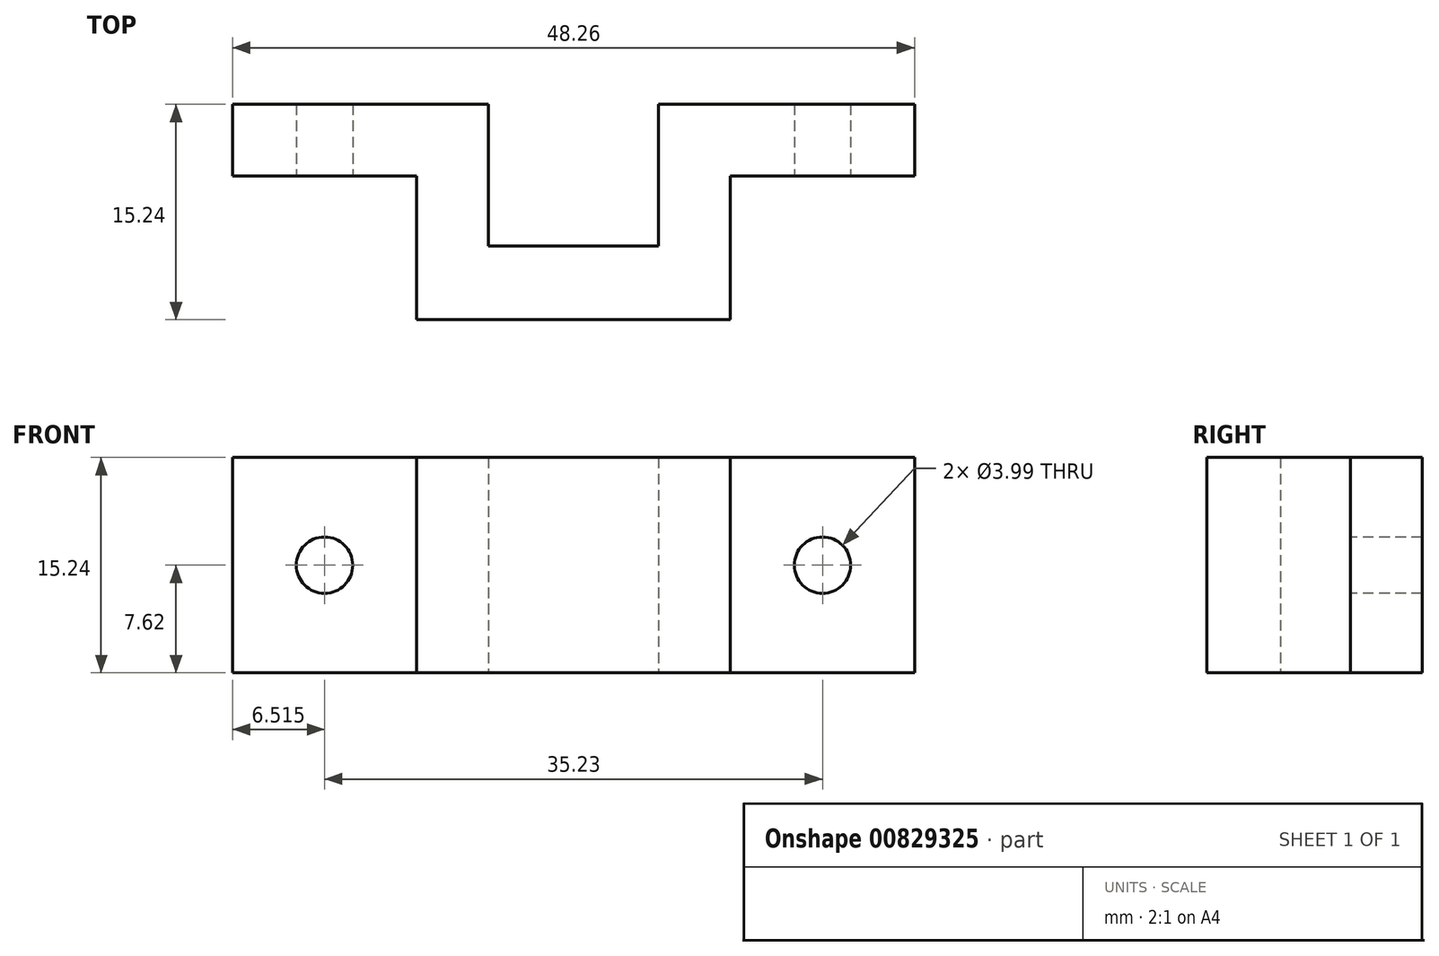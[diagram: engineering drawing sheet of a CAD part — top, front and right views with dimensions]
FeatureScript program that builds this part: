
annotation { "Feature Type Name" : "Feature", "Feature Type Description" : "" }
export const myFeature = defineFeature(function(context is Context, id is Id, definition is map)
    precondition{}
    {
        {
            var Q0;
            Q0=qCreatedBy(makeId("Front.planeOp"),FACE);
            var sketch = newSketch(context, id + "F0", { "sketchPlane" : qUnion([Q0])});
            skLineSegment(sketch, "E0.bottom", {"start": v(-24.13, 7.62) * mm, "end": v(24.13, 7.62) * mm});
            skLineSegment(sketch, "E0.top", {"start": v(-24.13, -7.62) * mm, "end": v(24.13, -7.62) * mm});
            skLineSegment(sketch, "E0.left", {"start": v(-24.13, 7.62) * mm, "end": v(-24.13, -7.62) * mm});
            skLineSegment(sketch, "E0.right", {"start": v(24.13, 7.62) * mm, "end": v(24.13, -7.62) * mm});
            skSolve(sketch);
        }
        {
            var Q0;
            Q0=makeQuery(id+"F0.imprint","IMPRINT",FACE,{"disambiguationData":[TD([[makeQuery(id+"F0.imprint","IMPRINT",EDGE,{"derivedFrom":sQuery(id+"F0.wireOp",EDGE,"E0.bottom")}),-1.0]])]});
            extrude(context, id + "F1", {"entities" : qUnion([Q0]), "depth" : 15.24 * mm, "offsetDistance" : 25.4 * mm});
        }
        {
            var Q0;
            Q0=makeQuery(id+"F1.opExtrude","SWEPT_FACE",FACE,{"disambiguationData":[OSD([sQuery(id+"F0.wireOp",EDGE,"E0.top")])]});
            var sketch = newSketch(context, id + "F2", { "sketchPlane" : qUnion([Q0])});
            skLineSegment(sketch, "E1.bottom", {"start": v(-6.02, 0) * mm, "end": v(6.02, 0) * mm});
            skLineSegment(sketch, "E1.top", {"start": v(-6.02, 10.03) * mm, "end": v(6.02, 10.03) * mm});
            skLineSegment(sketch, "E1.left", {"start": v(-6.02, 0) * mm, "end": v(-6.02, 10.03) * mm});
            skLineSegment(sketch, "E1.right", {"start": v(6.02, 0) * mm, "end": v(6.02, 10.03) * mm});
            skSolve(sketch);
        }
        {
            var Q0;
            Q0 = qSketchRegion(id + "F2", true);
            extrude(context, id + "F3", {"entities" : qUnion([Q0]), "operationType" : NewBodyOperationType.REMOVE, "oppositeDirection" : true, "depth" : 15.24 * mm, "offsetDistance" : 25.4 * mm});
        }
        {
            var Q0;
            Q0=makeQuery(id+"F1.opExtrude","SWEPT_FACE",FACE,{"disambiguationData":[OSD([sQuery(id+"F0.wireOp",EDGE,"E0.top")])]});
            var sketch = newSketch(context, id + "F4", { "sketchPlane" : qUnion([Q0])});
            skLineSegment(sketch, "E2.bottom", {"start": v(11.1, 15.24) * mm, "end": v(24.13, 15.24) * mm});
            skLineSegment(sketch, "E2.top", {"start": v(11.1, 5.07) * mm, "end": v(24.13, 5.07) * mm});
            skLineSegment(sketch, "E2.left", {"start": v(11.1, 15.24) * mm, "end": v(11.1, 5.07) * mm});
            skLineSegment(sketch, "E2.right", {"start": v(24.13, 15.24) * mm, "end": v(24.13, 5.07) * mm});
            skSolve(sketch);
        }
        {
            var Q0;
            Q0 = qSketchRegion(id + "F4", true);
            extrude(context, id + "F5", {"entities" : qUnion([Q0]), "operationType" : NewBodyOperationType.REMOVE, "oppositeDirection" : true, "depth" : 15.24 * mm, "offsetDistance" : 25.4 * mm});
        }
        {
            var Q0;
            Q0=makeQuery(id+"F1.opExtrude","SWEPT_FACE",FACE,{"disambiguationData":[OSD([sQuery(id+"F0.wireOp",EDGE,"E0.top")])]});
            var sketch = newSketch(context, id + "F6", { "sketchPlane" : qUnion([Q0])});
            skLineSegment(sketch, "E3.bottom", {"start": v(-24.13, 15.24) * mm, "end": v(-11.1, 15.24) * mm});
            skLineSegment(sketch, "E3.top", {"start": v(-24.13, 5.07) * mm, "end": v(-11.1, 5.07) * mm});
            skLineSegment(sketch, "E3.left", {"start": v(-24.13, 15.24) * mm, "end": v(-24.13, 5.07) * mm});
            skLineSegment(sketch, "E3.right", {"start": v(-11.1, 15.24) * mm, "end": v(-11.1, 5.07) * mm});
            skSolve(sketch);
        }
        {
            var Q0;
            Q0 = qSketchRegion(id + "F6", true);
            extrude(context, id + "F7", {"entities" : qUnion([Q0]), "operationType" : NewBodyOperationType.REMOVE, "oppositeDirection" : true, "depth" : 25.4 * mm, "offsetDistance" : 25.4 * mm});
        }
        {
            var Q0;
            Q0=makeQuery(id+"F7.boolean.opBoolean","COPY",FACE,{"derivedFrom":makeQuery(id+"F7.opExtrude","SWEPT_FACE",FACE,{"disambiguationData":[OSD([sQuery(id+"F6.wireOp",EDGE,"E3.top")])]})});
            var sketch = newSketch(context, id + "F8", { "sketchPlane" : qUnion([Q0])});
            skCircle(sketch, "E4", {"center": v(-17.61, 0) * mm, "radius": 2 * mm});
            skSolve(sketch);
        }
        {
            var Q0;
            Q0 = qSketchRegion(id + "F8", true);
            extrude(context, id + "F9", {"entities" : qUnion([Q0]), "operationType" : NewBodyOperationType.REMOVE, "oppositeDirection" : true, "depth" : 5.08 * mm, "offsetDistance" : 25.4 * mm});
        }
        {
            var Q0;
            Q0=makeQuery(id+"F5.boolean.opBoolean","COPY",FACE,{"derivedFrom":makeQuery(id+"F5.opExtrude","SWEPT_FACE",FACE,{"disambiguationData":[OSD([sQuery(id+"F4.wireOp",EDGE,"E2.top")])]})});
            var sketch = newSketch(context, id + "F10", { "sketchPlane" : qUnion([Q0])});
            skCircle(sketch, "E5", {"center": v(17.61, 0) * mm, "radius": 2 * mm});
            skSolve(sketch);
        }
        {
            var Q0;
            Q0 = qSketchRegion(id + "F10", true);
            extrude(context, id + "F11", {"entities" : qUnion([Q0]), "operationType" : NewBodyOperationType.REMOVE, "oppositeDirection" : true, "depth" : 5.08 * mm, "offsetDistance" : 25.4 * mm});
        }
    });
